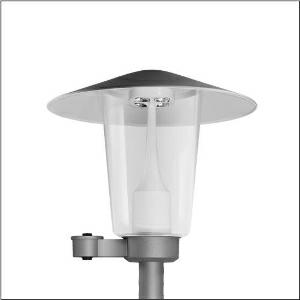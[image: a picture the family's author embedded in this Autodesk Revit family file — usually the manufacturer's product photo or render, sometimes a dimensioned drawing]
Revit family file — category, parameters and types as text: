
# Revit family: pilzleuchte_iq___st1_2a_5xa5235ey14h000022_5405
name_source: partatom
category: Lighting Fixtures
units: mm (PartAtom-declared; Revit-internal decimal feet)

## family parameters
Cut with Voids When Loaded = No
Host = Face
Light Source = No
Part Type = Normal
Room Calculation Point = No
Round Connector Dimension = Use Diameter
Shared = No

## types (1)
- --- (1 x LED, 1550 lm, 10.7 W, 3000K)
    Apparent Load = 11 VA
    CIE Flux Codes = 24 61 93 98 100
    Color Rendering = 70
    Color Temperature = 3000K
    Default Elevation = 1800 mm
    Description = Mushroom Luminaire iQ, mast luminaire, Module 540 iQ-SR, primary light control with 3 zone facetted reflector, of plastic, silver coated, highly specular, structured, primary optical cover: cover, of PMMA, transparent, light distribution: ST1.2a, light emission: direct distribution, primary light characteristic: asymmetric, installation type: post-top, LED, High Power LED, rated luminous flux: 1.550lm, luminous efficacy: 145lm/W, light colour: 730, colour temperature: 3000K, control gear: iQ-Street Remote, D4i with power reduction, control: optimised constant luminous flux control (CLO 2.0), Desk-Remote (wireless, voltage-free reading and setting of iQ features in the workshop via application-optimized NFC function/RFID function), Light-Fading, Smart-Wire, Night-Set, Lumen-Switch, Temp-Guard, Auto-Match, Street-Remote, pre-setting: logarithmic dimming characteristic, with terminal, 6-pole, max. 2.5mm², mains connection: 230..240V, AC, 50/60Hz, connection cable pre-assembled, cable length: 5,5m, wiring characteristics: H07RN-F, start of lifetime: 11W, end of service life: 11W, reduction: 6W, luminaire housing, upper part, of glass-fibre reinforced polyester, coated, SITECO metallic grey (DB 702S), diameter: 650mm, height: 586mm, spigot size: d x l = 76 x 70mm (post-top) | with reducer (optional accessory) 60 x 70mm, mounting height: 3..5m, post-top mast mounting element, of diecast aluminium, coated, SITECO metallic grey (DB 702S), Module 540 iQ-SR, traffic white (RAL 9016), equipment: standard, Smart Interface below and above, protection rating (complete): IP65, insulation class (complete): insulation class II (safety insulation), certification: CE, ENEC, VDE, packaging unit: 1 piece

Light Distribution: ST1.2a
    Height = 586 mm
    Lamp = 1 x LED
    Lamp Light Flux = 1550 lm
    Lamp Power = 10.7 W
    Lamp count = 1
    Length = 650 mm
    Luminous efficacy = 145 lm/W
    Manufacturer = Siteco
    ModVariant = No
    Model = 5XA5235EY14H000022
    Number of Poles = 1
    OnlyDefault = Yes
    Power Factor = 1
    Product Name = Pilzleuchte iQ | ST1.2a
    Product group = mast luminaire | pylon top
    ProductGroupID = 6100
    Protection Class = Protection class II
    Protection Degree = IP 65
    RLX_Detail_Level = 1
    RLX_Emergency_Light_Flux = 0 lm
    RLX_Emergency_Type = 0
    RLX_Emergency_Type_DB = No
    RlxData = <blob elided: 51737 chars, md5=02024db2>
    Socket = socket
    Standby Power = 0 W
    System Light Flux = 1550 lm
    System Power = 11 W
    Type Comments = factory setting: luminous flux: 100 % | dim-lin: 254 | 419 mA
    Type Image = l_1006957.jpg
    URL = http://relux.com
    VarID = @adj_091163
    Voltage = 0 V
    Weight = 0.00 kg
    Width = 0 mm  [stored 0 ft]

note: [stored X ft] marks values corroborated as IEEE doubles in the binary element streams (Revit-internal decimal feet)

## geometry (parser evidence)
native form markers: Blend x4, Sweep x13
no freeform markers — native parametric forms only
